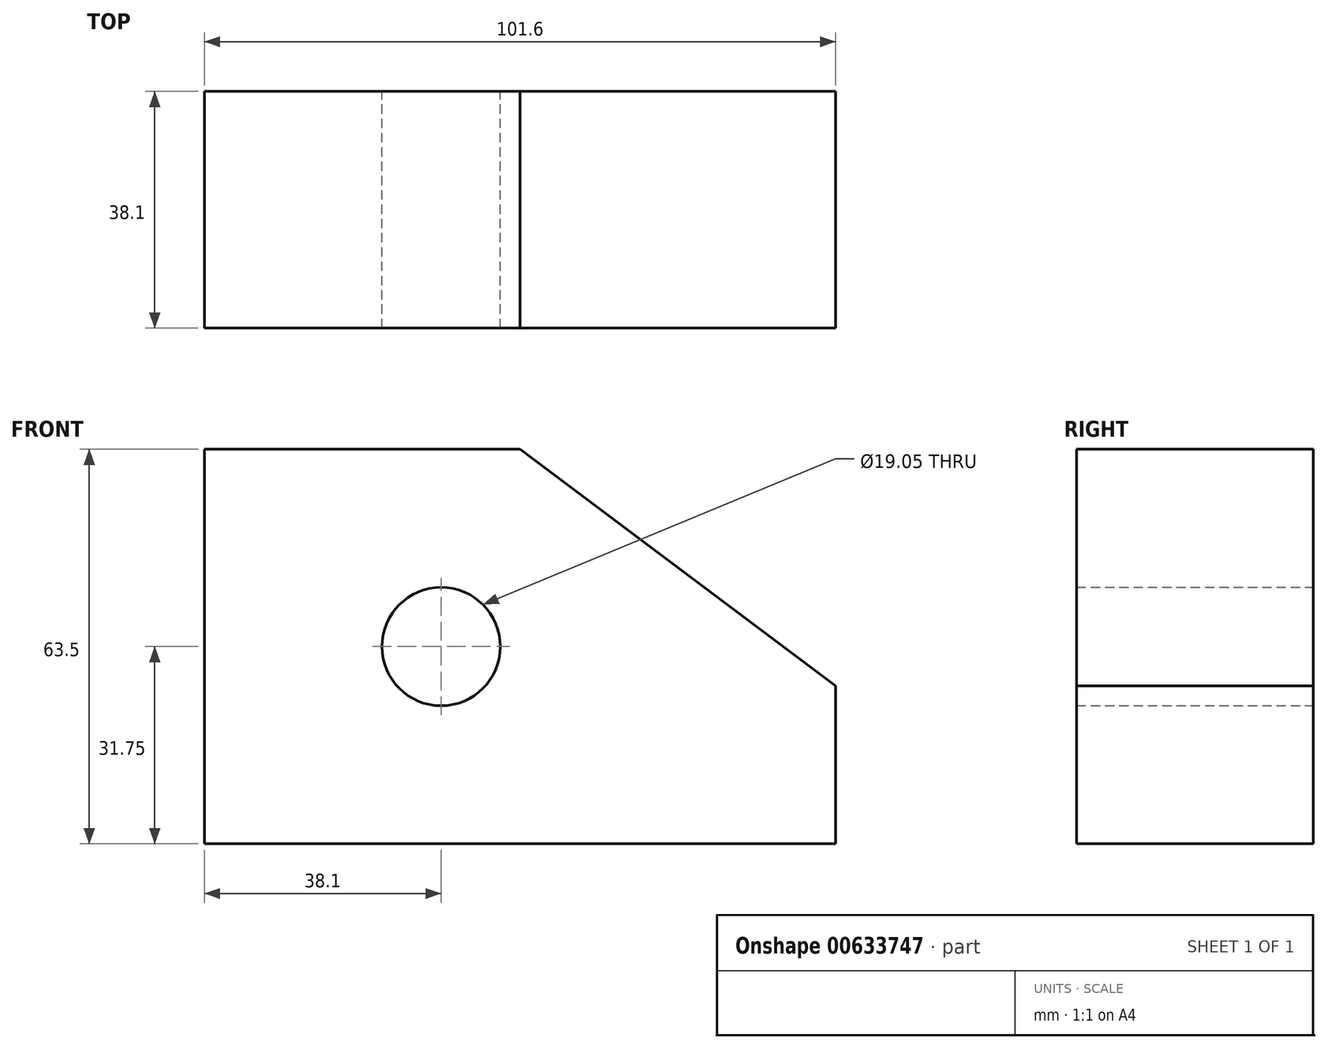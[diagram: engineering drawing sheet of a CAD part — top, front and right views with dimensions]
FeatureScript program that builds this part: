
annotation { "Feature Type Name" : "Feature", "Feature Type Description" : "" }
export const myFeature = defineFeature(function(context is Context, id is Id, definition is map)
    precondition{}
    {
        {
            var Q0;
            Q0=qCreatedBy(makeId("Front.planeOp"),FACE);
            var sketch = newSketch(context, id + "F0", { "sketchPlane" : qUnion([Q0])});
            skLineSegment(sketch, "E0", {"start": v(0, 0) * mm, "end": v(101.6, 0) * mm});
            skLineSegment(sketch, "E1", {"start": v(101.6, 0) * mm, "end": v(101.6, 25.4) * mm});
            skLineSegment(sketch, "E2", {"start": v(0, 0) * mm, "end": v(0, 63.5) * mm});
            skLineSegment(sketch, "E3", {"start": v(0, 63.5) * mm, "end": v(50.8, 63.5) * mm});
            skLineSegment(sketch, "E4", {"start": v(50.8, 63.5) * mm, "end": v(101.6, 25.4) * mm});
            skCircle(sketch, "E5", {"center": v(38.1, 31.75) * mm, "radius": 9.53 * mm});
            skSolve(sketch);
        }
        {
            var Q0;
            Q0=makeQuery(id+"F0.imprint","IMPRINT",FACE,{"disambiguationData":[TD([[makeQuery(id+"F0.imprint","IMPRINT",EDGE,{"derivedFrom":sQuery(id+"F0.wireOp",EDGE,"E0")}),1.0]])]});
            extrude(context, id + "F1", {"entities" : qUnion([Q0]), "depth" : 38.1 * mm, "offsetDistance" : 25.4 * mm});
        }
    });
